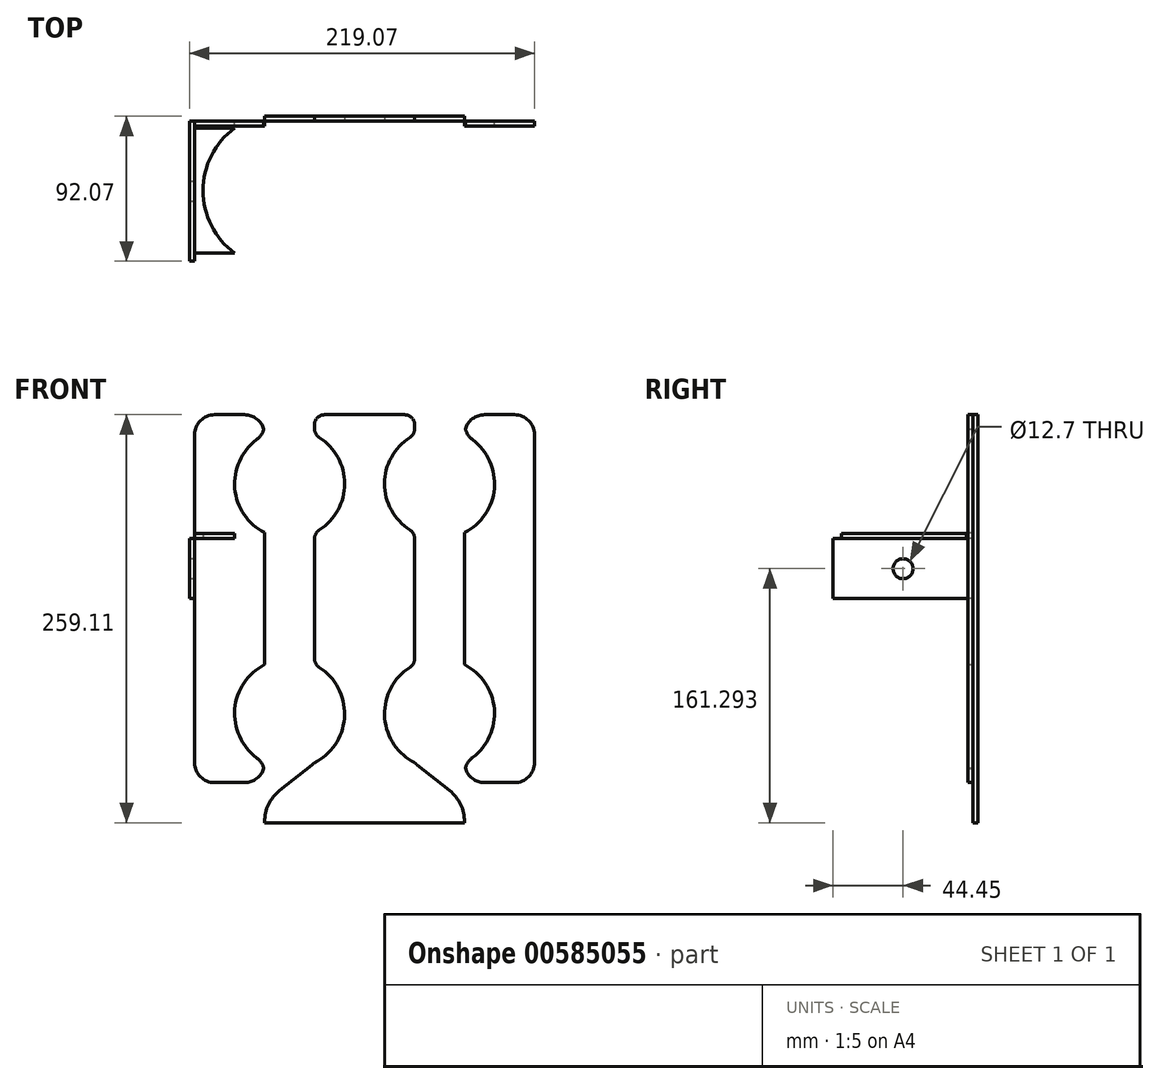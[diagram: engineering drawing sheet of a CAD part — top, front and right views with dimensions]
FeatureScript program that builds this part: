
annotation { "Feature Type Name" : "Feature", "Feature Type Description" : "" }
export const myFeature = defineFeature(function(context is Context, id is Id, definition is map)
    precondition{}
    {
        {
            var Q0;
            Q0=qCreatedBy(makeId("Front.planeOp"),FACE);
            var sketch = newSketch(context, id + "F0", { "sketchPlane" : qUnion([Q0])});
            skLineSegment(sketch, "E0.left", {"start": v(-44.45, 0) * mm, "end": v(0, 0) * mm, "construction": true});
            skPoint(sketch, "E0.middle", {"position": v(-25.4, 228.85) * mm});
            skCircle(sketch, "E1", {"center": v(-60.32, 56.5) * mm, "radius": 34.92 * mm, "construction": true});
            skLineSegment(sketch, "E2", {"start": v(-44.45, 0) * mm, "end": v(-44.45, 25.4) * mm});
            skLineSegment(sketch, "E3", {"start": v(-44.45, 25.4) * mm, "end": v(-5.12, 25.4) * mm, "construction": true});
            skLineSegment(sketch, "E4.trimOffspring", {"start": v(-44.45, 87.62) * mm, "end": v(-44.45, 171.45) * mm});
            skLineSegment(sketch, "E5.trimOffspring", {"start": v(-44.45, 233.67) * mm, "end": v(-44.45, 259.07) * mm});
            skArc(sketch, "E6", {"start": v(-44.45, 233.67) * mm, "mid": v(-25.4, 202.56) * mm, "end": v(-44.45, 171.45) * mm});
            skArc(sketch, "E7", {"start": v(-44.45, 87.62) * mm, "mid": v(-25.4, 56.5) * mm, "end": v(-44.45, 25.4) * mm});
            skLineSegment(sketch, "E8", {"start": v(-44.45, 259.07) * mm, "end": v(0, 259.07) * mm, "construction": true});
            skLineSegment(sketch, "E9", {"start": v(-25.4, 56.5) * mm, "end": v(-4.42, 56.5) * mm, "construction": true});
            skLineSegment(sketch, "E10.right", {"start": v(-139.7, 259.04) * mm, "end": v(-76.2, 259.04) * mm});
            skLineSegment(sketch, "E11", {"start": v(-139.7, 233.64) * mm, "end": v(-102.65, 233.64) * mm, "construction": true});
            skLineSegment(sketch, "E12.trimOffspring", {"start": v(-139.7, 87.6) * mm, "end": v(-139.7, 171.41) * mm});
            skLineSegment(sketch, "E13.trimOffspring", {"start": v(-139.7, 233.64) * mm, "end": v(-139.7, 259.04) * mm});
            skArc(sketch, "E14", {"start": v(-139.7, 87.6) * mm, "mid": v(-120.63, 56.48) * mm, "end": v(-139.7, 25.37) * mm});
            skArc(sketch, "E15", {"start": v(-139.7, 233.64) * mm, "mid": v(-120.63, 202.53) * mm, "end": v(-139.7, 171.41) * mm});
            skLineSegment(sketch, "E16", {"start": v(-139.7, 0) * mm, "end": v(-76.2, 0) * mm});
            skLineSegment(sketch, "E17", {"start": v(-76.2, 0) * mm, "end": v(-76.2, 25.4) * mm});
            skLineSegment(sketch, "E18", {"start": v(-139.7, 25.37) * mm, "end": v(-139.7, 0) * mm});
            skLineSegment(sketch, "E19", {"start": v(-95.25, 56.5) * mm, "end": v(-115.03, 56.5) * mm, "construction": true});
            skLineSegment(sketch, "E20", {"start": v(-95.25, 202.56) * mm, "end": v(-116.15, 202.56) * mm, "construction": true});
            skLineSegment(sketch, "E21.right", {"start": v(-171.45, -0.04) * mm, "end": v(-215.9, -0.04) * mm});
            skLineSegment(sketch, "E22", {"start": v(-171.45, 25.36) * mm, "end": v(-208.5, 25.36) * mm, "construction": true});
            skLineSegment(sketch, "E23.trimOffspring", {"start": v(-171.45, 171.42) * mm, "end": v(-171.45, 87.6) * mm});
            skArc(sketch, "E24", {"start": v(-171.45, 171.42) * mm, "mid": v(-190.5, 202.53) * mm, "end": v(-171.45, 233.64) * mm});
            skArc(sketch, "E25", {"start": v(-171.45, 25.36) * mm, "mid": v(-190.51, 56.48) * mm, "end": v(-171.45, 87.6) * mm});
            skLineSegment(sketch, "E26", {"start": v(-171.45, 259.04) * mm, "end": v(-215.9, 259.04) * mm, "construction": true});
            skLineSegment(sketch, "E27", {"start": v(-215.9, -0.04) * mm, "end": v(-215.9, 259.04) * mm});
            skLineSegment(sketch, "E28", {"start": v(-171.45, 233.64) * mm, "end": v(-171.45, 259.04) * mm});
            skCircle(sketch, "E29", {"center": v(-155.56, 56.48) * mm, "radius": 34.93 * mm, "construction": true});
            skCircle(sketch, "E30", {"center": v(-155.56, 202.53) * mm, "radius": 34.92 * mm, "construction": true});
            skLineSegment(sketch, "E31", {"start": v(0, 0) * mm, "end": v(0, 259.07) * mm});
            skArc(sketch, "E32", {"start": v(-76.2, 87.62) * mm, "mid": v(-95.25, 56.5) * mm, "end": v(-76.2, 25.4) * mm});
            skArc(sketch, "E33", {"start": v(-76.2, 233.66) * mm, "mid": v(-95.25, 202.56) * mm, "end": v(-76.2, 171.45) * mm});
            skLineSegment(sketch, "E34.trimOffspring", {"start": v(-76.2, 87.62) * mm, "end": v(-76.2, 171.45) * mm});
            skLineSegment(sketch, "E35.trimOffspring", {"start": v(-76.2, 233.66) * mm, "end": v(-76.2, 259.04) * mm, "construction": true});
            skLineSegment(sketch, "E36.0", {"start": v(-44.45, 12.7) * mm, "end": v(0, 12.7) * mm});
            skLineSegment(sketch, "E37.0", {"start": v(-12.7, 0) * mm, "end": v(-12.7, 259.07) * mm, "construction": true});
            skLineSegment(sketch, "E38.0", {"start": v(-139.7, 12.7) * mm, "end": v(-76.2, 12.7) * mm, "construction": true});
            skLineSegment(sketch, "E39.0", {"start": v(-171.45, 12.66) * mm, "end": v(-215.9, 12.66) * mm});
            skLineSegment(sketch, "E40.0", {"start": v(-203.2, -0.04) * mm, "end": v(-203.2, 259.04) * mm, "construction": true});
            skCircle(sketch, "E41", {"center": v(-203.2, 12.66) * mm, "radius": 4.76 * mm, "construction": true});
            skCircle(sketch, "E42", {"center": v(-107.95, 12.7) * mm, "radius": 4.76 * mm, "construction": true});
            skCircle(sketch, "E43", {"center": v(-12.7, 12.7) * mm, "radius": 4.76 * mm, "construction": true});
            skLineSegment(sketch, "E44.bottom", {"start": v(-171.45, 259.04) * mm, "end": v(-177.8, 259.04) * mm, "construction": true});
            skLineSegment(sketch, "E44.top", {"start": v(-171.45, 246.34) * mm, "end": v(-177.8, 246.34) * mm, "construction": true});
            skLineSegment(sketch, "E44.left", {"start": v(-171.45, 259.04) * mm, "end": v(-171.45, 246.34) * mm, "construction": true});
            skLineSegment(sketch, "E44.right", {"start": v(-177.8, 259.04) * mm, "end": v(-177.8, 246.34) * mm, "construction": true});
            skLineSegment(sketch, "E45.bottom", {"start": v(-139.7, 259.04) * mm, "end": v(-133.34, 259.04) * mm, "construction": true});
            skLineSegment(sketch, "E45.top", {"start": v(-139.7, 246.34) * mm, "end": v(-133.34, 246.34) * mm, "construction": true});
            skLineSegment(sketch, "E45.left", {"start": v(-139.7, 259.04) * mm, "end": v(-139.7, 246.34) * mm, "construction": true});
            skLineSegment(sketch, "E45.right", {"start": v(-133.34, 259.04) * mm, "end": v(-133.34, 246.34) * mm, "construction": true});
            skLineSegment(sketch, "E46.bottom", {"start": v(-76.2, 259.04) * mm, "end": v(-82.55, 259.04) * mm, "construction": true});
            skLineSegment(sketch, "E46.top", {"start": v(-76.2, 246.34) * mm, "end": v(-82.55, 246.34) * mm, "construction": true});
            skLineSegment(sketch, "E46.left", {"start": v(-76.2, 259.04) * mm, "end": v(-76.2, 246.34) * mm, "construction": true});
            skLineSegment(sketch, "E46.right", {"start": v(-82.55, 259.04) * mm, "end": v(-82.55, 246.34) * mm, "construction": true});
            skLineSegment(sketch, "E47.bottom", {"start": v(-44.45, 259.07) * mm, "end": v(-38.1, 259.07) * mm, "construction": true});
            skLineSegment(sketch, "E47.top", {"start": v(-44.45, 246.37) * mm, "end": v(-38.1, 246.37) * mm, "construction": true});
            skLineSegment(sketch, "E47.left", {"start": v(-44.45, 259.07) * mm, "end": v(-44.45, 246.37) * mm, "construction": true});
            skLineSegment(sketch, "E47.right", {"start": v(-38.1, 259.07) * mm, "end": v(-38.1, 246.37) * mm, "construction": true});
            skCircle(sketch, "E48", {"center": v(-177.8, 246.34) * mm, "radius": 3.18 * mm, "construction": true});
            skCircle(sketch, "E49", {"center": v(-133.34, 246.34) * mm, "radius": 3.18 * mm, "construction": true});
            skCircle(sketch, "E50", {"center": v(-82.55, 246.34) * mm, "radius": 3.18 * mm, "construction": true});
            skCircle(sketch, "E51", {"center": v(-38.1, 246.37) * mm, "radius": 3.17 * mm, "construction": true});
            skLineSegment(sketch, "E52", {"start": v(-124.8, 219.06) * mm, "end": v(-91.1, 219.06) * mm, "construction": true});
            skLineSegment(sketch, "E53.0", {"start": v(-184.15, 25.36) * mm, "end": v(-184.15, -0.04) * mm, "construction": true});
            skLineSegment(sketch, "E54", {"start": v(-31.75, 36.42) * mm, "end": v(-31.75, 36.52) * mm});
            skCircle(sketch, "E55", {"center": v(-60.32, 202.56) * mm, "radius": 34.93 * mm, "construction": true});
            skArc(sketch, "E56", {"start": v(-76.2, 171.45) * mm, "mid": v(-93.65, 192.13) * mm, "end": v(-91.1, 219.06) * mm});
            skArc(sketch, "E57", {"start": v(-124.8, 219.06) * mm, "mid": v(-122.22, 192.1) * mm, "end": v(-139.7, 171.41) * mm});
            skLineSegment(sketch, "E58", {"start": v(-171.45, 25.36) * mm, "end": v(-171.45, 12.66) * mm});
            skLineSegment(sketch, "E59", {"start": v(0, 246.37) * mm, "end": v(-44.45, 246.37) * mm});
            skPoint(sketch, "E59.startSnap0", {"position": v(-44.45, 246.37) * mm});
            skLineSegment(sketch, "E60", {"start": v(-171.45, 246.34) * mm, "end": v(-215.9, 246.34) * mm});
            skSolve(sketch);
        }
        {
            var Q0;
            Q0 = qSketchRegion(id + "F0", true);
            extrude(context, id + "F1", {"entities" : qUnion([Q0]), "depth" : 3.17 * mm, "offsetDistance" : 25.4 * mm});
        }
        {
            var Q0;
            Q0=makeQuery(id+"F1.opExtrude","SWEPT_EDGE",EDGE,{"disambiguationData":[OSD([sQuery(id+"F0.wireOp",EDGE,"E26"),sQuery(id+"F0.wireOp",EDGE,"E27")])]});
            var Q1;
            Q1=makeQuery(id+"F1.opExtrude","SWEPT_EDGE",EDGE,{"disambiguationData":[OSD([sQuery(id+"F0.wireOp",EDGE,"E10.right"),sQuery(id+"F0.wireOp",EDGE,"E13.trimOffspring")])]});
            var Q2;
            Q2=makeQuery(id+"F1.opExtrude","SWEPT_EDGE",EDGE,{"disambiguationData":[OSD([sQuery(id+"F0.wireOp",EDGE,"E10.right"),sQuery(id+"F0.wireOp",EDGE,"E35.trimOffspring")])]});
            var Q3;
            Q3=makeQuery(id+"F1.opExtrude","SWEPT_EDGE",EDGE,{"disambiguationData":[OSD([sQuery(id+"F0.wireOp",EDGE,"E5.trimOffspring"),sQuery(id+"F0.wireOp",EDGE,"E8")])]});
            var Q4;
            Q4=makeQuery(id+"F1.opExtrude","SWEPT_EDGE",EDGE,{"disambiguationData":[OSD([sQuery(id+"F0.wireOp",EDGE,"E8"),sQuery(id+"F0.wireOp",EDGE,"E31")])]});
            var Q5;
            Q5=makeQuery(id+"F1.opExtrude","SWEPT_EDGE",EDGE,{"disambiguationData":[OSD([sQuery(id+"F0.wireOp",EDGE,"E0.left"),sQuery(id+"F0.wireOp",EDGE,"E31")])]});
            var Q6;
            Q6=makeQuery(id+"F1.opExtrude","SWEPT_EDGE",EDGE,{"disambiguationData":[OSD([sQuery(id+"F0.wireOp",EDGE,"E0.left"),sQuery(id+"F0.wireOp",EDGE,"E2")])]});
            var Q7;
            Q7=makeQuery(id+"F1.opExtrude","SWEPT_EDGE",EDGE,{"disambiguationData":[OSD([sQuery(id+"F0.wireOp",EDGE,"E16"),sQuery(id+"F0.wireOp",EDGE,"E17")])]});
            var Q8;
            Q8=makeQuery(id+"F1.opExtrude","SWEPT_EDGE",EDGE,{"disambiguationData":[OSD([sQuery(id+"F0.wireOp",EDGE,"E16"),sQuery(id+"F0.wireOp",EDGE,"E18")])]});
            var Q9;
            Q9=makeQuery(id+"F1.opExtrude","SWEPT_EDGE",EDGE,{"disambiguationData":[OSD([sQuery(id+"F0.wireOp",EDGE,"E21.right"),sQuery(id+"F0.wireOp",EDGE,"2a9ababa-c8f5-4b90-8fbc-ec9f41eeb0cb.trimOffspring")])]});
            var Q10;
            Q10=makeQuery(id+"F1.opExtrude","SWEPT_EDGE",EDGE,{"disambiguationData":[OSD([sQuery(id+"F0.wireOp",EDGE,"E21.right"),sQuery(id+"F0.wireOp",EDGE,"E27")])]});
            var Q11;
            Q11=makeQuery(id+"F1.opExtrude","SWEPT_EDGE",EDGE,{"disambiguationData":[OSD([sQuery(id+"F0.wireOp",EDGE,"E26"),sQuery(id+"F0.wireOp",EDGE,"E28")])]});
            var Q12;
            Q12=makeQuery(id+"F1.opExtrude","SWEPT_EDGE",EDGE,{"disambiguationData":[OSD([sQuery(id+"F0.wireOp",EDGE,"E39.0"),sQuery(id+"F0.wireOp",EDGE,"E58")])]});
            var Q13;
            Q13=makeQuery(id+"F1.opExtrude","SWEPT_EDGE",EDGE,{"disambiguationData":[OSD([sQuery(id+"F0.wireOp",EDGE,"E25"),sQuery(id+"F0.wireOp",EDGE,"E58")])]});
            fillet(context, id + "F2", {"entities" : qUnion([Q0, Q1, Q2, Q3, Q4, Q5, Q6, Q7, Q8, Q9, Q10, Q11, Q12, Q13]), "tangentPropagation" : true, "radius" : 12.7 * mm, "defaultsChanged" : false, "vertexSettings" : [], "allowEdgeOverflow" : false});
        }
        {
            var Q0;
            Q0=qCreatedBy(makeId("Front.planeOp"),FACE);
            var sketch = newSketch(context, id + "F3", { "sketchPlane" : qUnion([Q0])});
            skLineSegment(sketch, "E61.trimOffspring", {"start": v(-139.7, 87.58) * mm, "end": v(-139.7, 171.4) * mm});
            skArc(sketch, "E62", {"start": v(-139.7, 87.58) * mm, "mid": v(-120.63, 56.47) * mm, "end": v(-139.7, 25.36) * mm});
            skArc(sketch, "E63", {"start": v(-76.2, 87.6) * mm, "mid": v(-95.25, 56.5) * mm, "end": v(-76.2, 25.39) * mm});
            skLineSegment(sketch, "E64.trimOffspring", {"start": v(-76.2, 87.6) * mm, "end": v(-76.2, 171.44) * mm});
            skArc(sketch, "E65", {"start": v(-139.7, 171.4) * mm, "mid": v(-120.63, 202.52) * mm, "end": v(-139.7, 233.63) * mm});
            skArc(sketch, "E66", {"start": v(-76.2, 171.44) * mm, "mid": v(-95.25, 202.55) * mm, "end": v(-76.2, 233.65) * mm});
            skLineSegment(sketch, "E67.top", {"start": v(-139.7, 246.35) * mm, "end": v(-76.2, 246.35) * mm});
            skLineSegment(sketch, "E67.left", {"start": v(-139.7, 233.63) * mm, "end": v(-139.7, 246.35) * mm});
            skLineSegment(sketch, "E67.right", {"start": v(-76.2, 233.63) * mm, "end": v(-76.2, 246.35) * mm});
            skLineSegment(sketch, "E68", {"start": v(-107.95, 17.58) * mm, "end": v(-107.95, -12.74) * mm, "construction": true});
            skLineSegment(sketch, "E69", {"start": v(-107.95, -12.74) * mm, "end": v(-171.45, -12.74) * mm});
            skLineSegment(sketch, "E70", {"start": v(-171.45, -12.74) * mm, "end": v(-171.45, -0.04) * mm});
            skLineSegment(sketch, "E71", {"start": v(-139.7, 25.36) * mm, "end": v(-171.45, -0.04) * mm});
            skLineSegment(sketch, "E72.MirrorCS", {"start": v(-44.45, -12.74) * mm, "end": v(-44.45, -0.04) * mm});
            skLineSegment(sketch, "E73.MirrorCS", {"start": v(-107.95, -12.74) * mm, "end": v(-44.45, -12.74) * mm});
            skLineSegment(sketch, "E74", {"start": v(-76.2, 25.39) * mm, "end": v(-44.45, -0.04) * mm});
            skSolve(sketch);
        }
        {
            var Q0;
            Q0 = qSketchRegion(id + "F3", true);
            extrude(context, id + "F4", {"entities" : qUnion([Q0]), "oppositeDirection" : true, "depth" : 3.17 * mm, "offsetDistance" : 25.4 * mm});
        }
        {
            var Q0;
            Q0=makeQuery(id+"F4.opExtrude","SWEPT_EDGE",EDGE,{"disambiguationData":[OSD([sQuery(id+"F3.wireOp",EDGE,"E70"),sQuery(id+"F3.wireOp",EDGE,"E71")])]});
            var Q1;
            Q1=makeQuery(id+"F4.opExtrude","SWEPT_EDGE",EDGE,{"disambiguationData":[OSD([sQuery(id+"F3.wireOp",EDGE,"E62"),sQuery(id+"F3.wireOp",EDGE,"E71")])]});
            var Q2;
            Q2=makeQuery(id+"F4.opExtrude","SWEPT_EDGE",EDGE,{"disambiguationData":[OSD([sQuery(id+"F3.wireOp",EDGE,"E63"),sQuery(id+"F3.wireOp",EDGE,"E74")])]});
            var Q3;
            Q3=makeQuery(id+"F4.opExtrude","SWEPT_EDGE",EDGE,{"disambiguationData":[OSD([sQuery(id+"F3.wireOp",EDGE,"E72.MirrorCS"),sQuery(id+"F3.wireOp",EDGE,"E74")])]});
            fillet(context, id + "F5", {"entities" : qUnion([Q0, Q1, Q2, Q3]), "tangentPropagation" : true, "radius" : 25.4 * mm, "defaultsChanged" : false, "vertexSettings" : [], "allowEdgeOverflow" : false});
        }
        {
            var Q0;
            Q0=makeQuery(id+"F4.opExtrude","SWEPT_EDGE",EDGE,{"disambiguationData":[OSD([sQuery(id+"F3.wireOp",EDGE,"E67.top"),sQuery(id+"F3.wireOp",EDGE,"E67.left")])]});
            var Q1;
            Q1=makeQuery(id+"F4.opExtrude","SWEPT_EDGE",EDGE,{"disambiguationData":[OSD([sQuery(id+"F3.wireOp",EDGE,"E67.top"),sQuery(id+"F3.wireOp",EDGE,"E67.right")])]});
            var Q2;
            Q2=makeQuery(id+"F4.opExtrude","SWEPT_EDGE",EDGE,{"disambiguationData":[OSD([sQuery(id+"F3.wireOp",EDGE,"E66"),sQuery(id+"F3.wireOp",EDGE,"E67.right")])]});
            var Q3;
            Q3=makeQuery(id+"F4.opExtrude","SWEPT_EDGE",EDGE,{"disambiguationData":[OSD([sQuery(id+"F3.wireOp",EDGE,"E65"),sQuery(id+"F3.wireOp",EDGE,"E67.left")])]});
            var Q4;
            Q4=makeQuery(id+"F4.opExtrude","SWEPT_EDGE",EDGE,{"disambiguationData":[OSD([sQuery(id+"F3.wireOp",EDGE,"E61.trimOffspring"),sQuery(id+"F3.wireOp",EDGE,"E65")])]});
            var Q5;
            Q5=makeQuery(id+"F4.opExtrude","SWEPT_EDGE",EDGE,{"disambiguationData":[OSD([sQuery(id+"F3.wireOp",EDGE,"E64.trimOffspring"),sQuery(id+"F3.wireOp",EDGE,"E66")])]});
            var Q6;
            Q6=makeQuery(id+"F4.opExtrude","SWEPT_EDGE",EDGE,{"disambiguationData":[OSD([sQuery(id+"F3.wireOp",EDGE,"E63"),sQuery(id+"F3.wireOp",EDGE,"E64.trimOffspring")])]});
            var Q7;
            Q7=makeQuery(id+"F4.opExtrude","SWEPT_EDGE",EDGE,{"disambiguationData":[OSD([sQuery(id+"F3.wireOp",EDGE,"E61.trimOffspring"),sQuery(id+"F3.wireOp",EDGE,"E62")])]});
            fillet(context, id + "F6", {"entities" : qUnion([Q0, Q1, Q2, Q3, Q4, Q5, Q6, Q7]), "tangentPropagation" : true, "radius" : 6.35 * mm, "defaultsChanged" : false, "vertexSettings" : [], "allowEdgeOverflow" : false});
        }
        {
            var Q0;
            Q0=makeQuery(id+"F1.opExtrude","SWEPT_FACE",FACE,{"disambiguationData":[OSD([sQuery(id+"F0.wireOp",EDGE,"E27")])]});
            var sketch = newSketch(context, id + "F7", { "sketchPlane" : qUnion([Q0])});
            skLineSegment(sketch, "E75.bottom", {"start": v(0, 129.5) * mm, "end": v(88.9, 129.5) * mm});
            skLineSegment(sketch, "E75.top", {"start": v(0, 167.6) * mm, "end": v(88.9, 167.6) * mm});
            skLineSegment(sketch, "E75.left", {"start": v(0, 129.5) * mm, "end": v(0, 167.6) * mm});
            skLineSegment(sketch, "E75.right", {"start": v(88.9, 129.5) * mm, "end": v(88.9, 167.6) * mm});
            skCircle(sketch, "E76", {"center": v(44.45, 148.55) * mm, "radius": 6.35 * mm});
            skPoint(sketch, "E76.centerSnap0", {"position": v(88.9, 148.55) * mm});
            skPoint(sketch, "E76.centerSnap1", {"position": v(44.45, 129.5) * mm});
            skSolve(sketch);
        }
        {
            var Q0;
            Q0 = qSketchRegion(id + "F7", true);
            extrude(context, id + "F8", {"entities" : qUnion([Q0]), "depth" : 3.17 * mm, "offsetDistance" : 25.4 * mm});
        }
        {
            var Q0;
            Q0=makeQuery(id+"F8.opExtrude","SWEPT_FACE",FACE,{"disambiguationData":[OSD([sQuery(id+"F7.wireOp",EDGE,"E75.top")])]});
            var sketch = newSketch(context, id + "F9", { "sketchPlane" : qUnion([Q0])});
            skLineSegment(sketch, "E77.bottom", {"start": v(-215.9, -4.34) * mm, "end": v(-190.5, -4.34) * mm});
            skLineSegment(sketch, "E77.top", {"start": v(-215.9, -83.72) * mm, "end": v(-190.5, -83.72) * mm});
            skLineSegment(sketch, "E77.left", {"start": v(-215.9, -4.34) * mm, "end": v(-215.9, -83.72) * mm});
            skArc(sketch, "E78", {"start": v(-190.5, -4.34) * mm, "mid": v(-210.53, -44.03) * mm, "end": v(-190.5, -83.72) * mm});
            skSolve(sketch);
        }
        {
            var Q0;
            Q0 = qSketchRegion(id + "F9", true);
            extrude(context, id + "F10", {"entities" : qUnion([Q0]), "depth" : 3.17 * mm, "offsetDistance" : 25.4 * mm});
        }
    });
